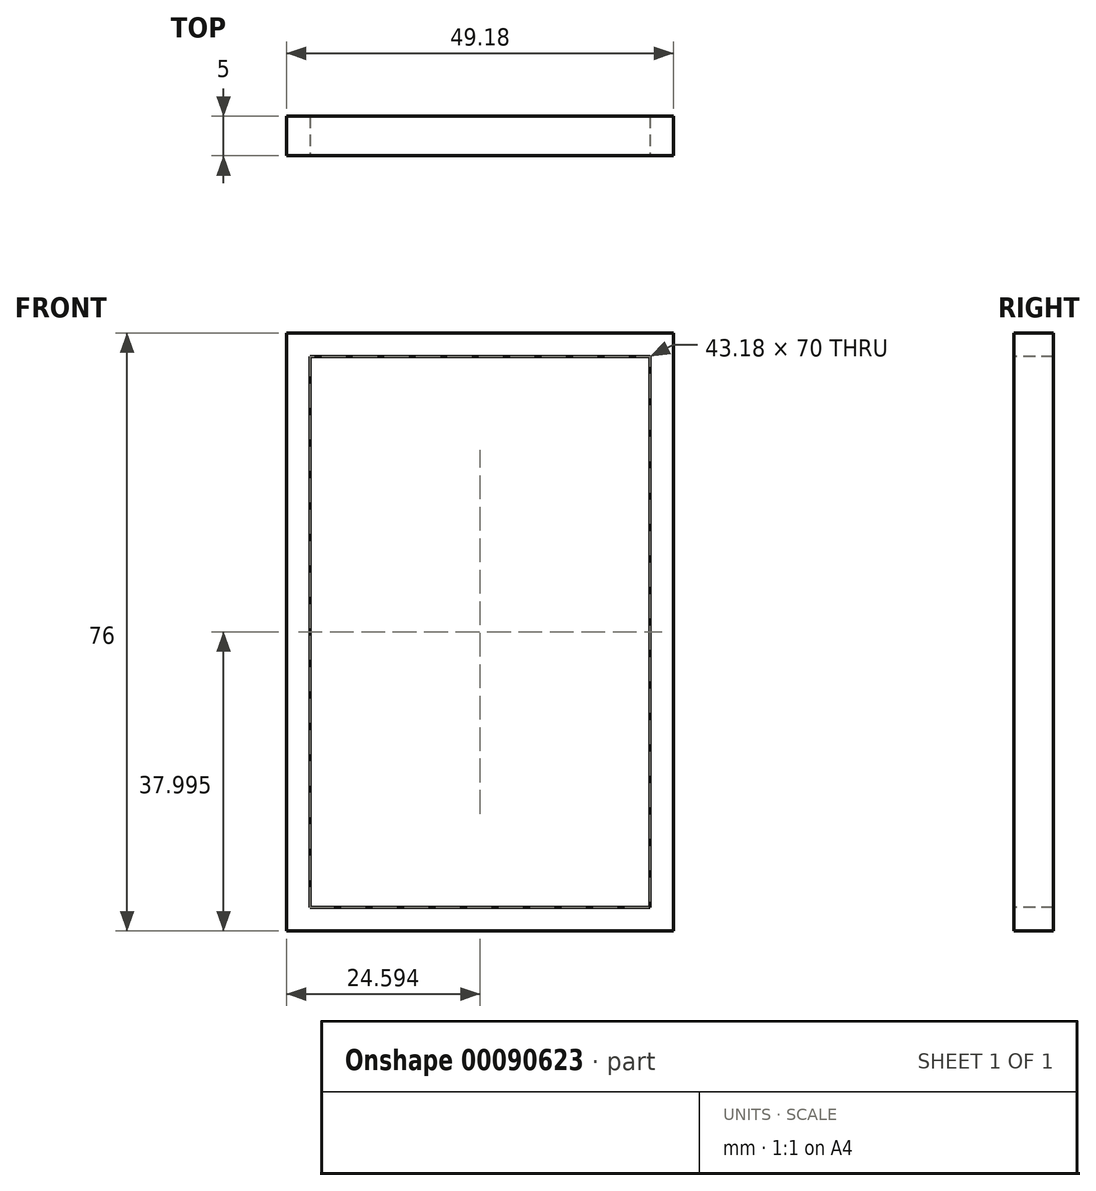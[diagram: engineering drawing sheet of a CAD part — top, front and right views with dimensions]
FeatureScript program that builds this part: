
annotation { "Feature Type Name" : "Feature", "Feature Type Description" : "" }
export const myFeature = defineFeature(function(context is Context, id is Id, definition is map)
    precondition{}
    {
        {
            var Q0;
            Q0=qCreatedBy(makeId("Front.planeOp"),FACE);
            var sketch = newSketch(context, id + "F0", { "sketchPlane" : qUnion([Q0])});
            skLineSegment(sketch, "E0.bottom", {"start": v(-23.22, 59.73) * mm, "end": v(25.96, 59.73) * mm});
            skLineSegment(sketch, "E0.top", {"start": v(-23.22, -16.27) * mm, "end": v(25.96, -16.27) * mm});
            skLineSegment(sketch, "E0.left", {"start": v(-23.22, 59.73) * mm, "end": v(-23.22, -16.27) * mm});
            skLineSegment(sketch, "E0.right", {"start": v(25.96, 59.73) * mm, "end": v(25.96, -16.27) * mm});
            skLineSegment(sketch, "E1.bottom", {"start": v(-20.22, 56.73) * mm, "end": v(22.96, 56.73) * mm});
            skLineSegment(sketch, "E1.top", {"start": v(-20.22, -13.27) * mm, "end": v(22.96, -13.27) * mm});
            skLineSegment(sketch, "E1.left", {"start": v(-20.22, 56.73) * mm, "end": v(-20.22, -13.27) * mm});
            skLineSegment(sketch, "E1.right", {"start": v(22.96, 56.73) * mm, "end": v(22.96, -13.27) * mm});
            skSolve(sketch);
        }
        {
            var Q0;
            Q0=makeQuery(id+"F0.imprint","IMPRINT",FACE,{"disambiguationData":[TD([[makeQuery(id+"F0.imprint","IMPRINT",EDGE,{"derivedFrom":sQuery(id+"F0.wireOp",EDGE,"E0.bottom")}),-1.0]])]});
            extrude(context, id + "F1", {"entities" : qUnion([Q0]), "oppositeDirection" : true, "depth" : 5 * mm});
        }
    });
